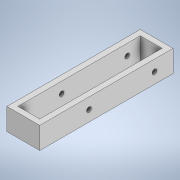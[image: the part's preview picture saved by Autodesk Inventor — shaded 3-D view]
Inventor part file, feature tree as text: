
AUTODESK INVENTOR PART (.ipt)
format: ipt  version: 2022 (Build 260153000, 153)  size: 126,464 bytes
history: native  units: mm
features: extrude x2, sketch x1
ambient origin geometry x8: Origin, YZ Plane, XZ Plane, XY Plane, X Axis, Y Axis, Z Axis, Center Point
bodies: Solid1 (feature_tree)
feature tree (3):
  extrude  "Extrusion1"  Depth=15.0mm
  extrude  "Extrusion2"  Depth=10.0mm
  sketch  "Sketch1"  dims[d0=60.0mm d1=15.0mm d2=5.0mm d3=5.0mm d4=2.5mm d5=2.5mm d6=10.0mm d7=0.0mm d8=10.0mm d10=0.0mm d11=0.0mm d12=1.0mm d13=1.0mm d14=20.0mm d15=2.2mm]
